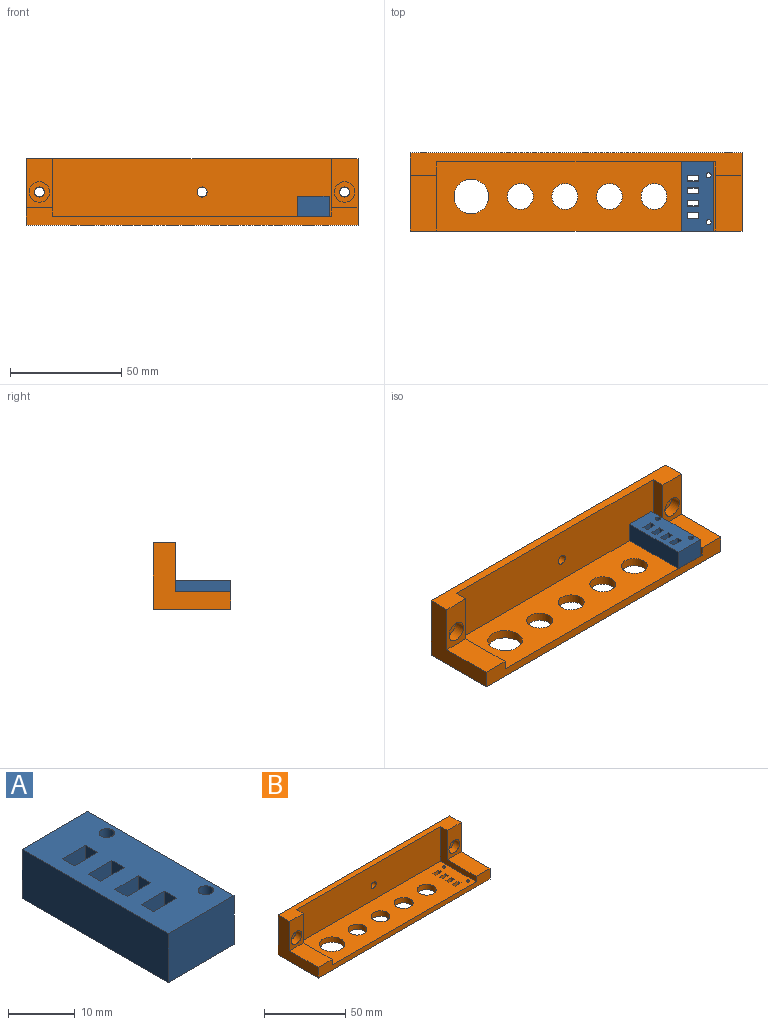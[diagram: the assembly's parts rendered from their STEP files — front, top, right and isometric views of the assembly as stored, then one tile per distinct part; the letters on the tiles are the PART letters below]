
ASSEMBLY  parts=2 mates=1
PART A: 44 faces, bbox 14x31x9 mm
  f0: plane 2.4x1mm, normal (1,0,0), area 2.4mm2, adj f1,f12,f23,f28
  f1: plane 4.8x1mm, normal (0,-1,0), area 4.8mm2, adj f0,f2,f23,f28
  f2: plane 2.4x1mm, normal (-1,0,0), area 2.4mm2, adj f1,f12,f23,f28
  f3: plane 2.4x1mm, normal (1,0,0), area 2.4mm2, adj f4,f13,f23,f33
  f4: plane 4.8x1mm, normal (0,-1,0), area 4.8mm2, adj f3,f5,f23,f33
  f5: plane 2.4x1mm, normal (-1,0,0), area 2.4mm2, adj f4,f13,f23,f33
  f6: plane 2.4x1mm, normal (1,0,0), area 2.4mm2, adj f7,f14,f23,f38
  f7: plane 4.8x1mm, normal (0,-1,0), area 4.8mm2, adj f6,f8,f23,f38
  f8: plane 2.4x1mm, normal (-1,0,0), area 2.4mm2, adj f7,f14,f23,f38
  f9: plane 2.4x1mm, normal (1,0,0), area 2.4mm2, adj f10,f15,f23,f43
  f10: plane 4.8x1mm, normal (0,-1,0), area 4.8mm2, adj f9,f11,f23,f43
  f11: plane 2.4x1mm, normal (-1,0,0), area 2.4mm2, adj f10,f15,f23,f43
  f12: plane 4.8x1mm, normal (0,1,0), area 4.8mm2, adj f0,f2,f23,f28
  f13: plane 4.8x1mm, normal (0,1,0), area 4.8mm2, adj f3,f5,f23,f33
  f14: plane 4.8x1mm, normal (0,1,0), area 4.8mm2, adj f6,f8,f23,f38
  f15: plane 4.8x1mm, normal (0,1,0), area 4.8mm2, adj f9,f11,f23,f43
  f16: plane 31x14mm, normal (0,0,1), area 373.7mm2, adj f17,f18,f19,f20,f21,f22,f24,f25
  f17: plane 14x9mm, normal (0,1,0), area 126mm2, adj f16,f18,f22,f23
  f18: plane 31x9mm, normal (-1,0,0), area 279mm2, adj f16,f17,f19,f23
  f19: plane 14x9mm, normal (0,-1,0), area 126mm2, adj f16,f18,f22,f23
  f20: cylinder r=1.15mm len=9mm, axis (0,0,-1), area 65mm2, adj f16,f23
  f21: cylinder r=1.15mm len=9mm, axis (0,0,-1), area 65mm2, adj f16,f23
  f22: plane 31x9mm, normal (1,0,0), area 279mm2, adj f16,f17,f19,f23
  f23: plane 31x14mm, normal (0,0,-1), area 379.6mm2, adj f0,f1,f2,f3,f4,f5,f6,f7
  f24: plane 8x5mm, normal (0,-1,0), area 40mm2, adj f16,f25,f27,f28
  f25: plane 8x2.6mm, normal (1,0,0), area 20.8mm2, adj f16,f24,f26,f28
  f26: plane 8x5mm, normal (0,1,0), area 40mm2, adj f16,f25,f27,f28
  f27: plane 8x2.6mm, normal (-1,0,0), area 20.8mm2, adj f16,f24,f26,f28
  f28: plane 5x2.6mm, normal (0,0,1), area 1.5mm2, adj f0,f1,f2,f12,f24,f25,f26,f27
  f29: plane 8x5mm, normal (0,-1,0), area 40mm2, adj f16,f30,f32,f33
  f30: plane 8x2.6mm, normal (1,0,0), area 20.8mm2, adj f16,f29,f31,f33
  f31: plane 8x5mm, normal (0,1,0), area 40mm2, adj f16,f30,f32,f33
  f32: plane 8x2.6mm, normal (-1,0,0), area 20.8mm2, adj f16,f29,f31,f33
  f33: plane 5x2.6mm, normal (0,0,1), area 1.5mm2, adj f3,f4,f5,f13,f29,f30,f31,f32
  f34: plane 8x5mm, normal (0,-1,0), area 40mm2, adj f16,f35,f37,f38
  f35: plane 8x2.6mm, normal (1,0,0), area 20.8mm2, adj f16,f34,f36,f38
  f36: plane 8x5mm, normal (0,1,0), area 40mm2, adj f16,f35,f37,f38
  f37: plane 8x2.6mm, normal (-1,0,0), area 20.8mm2, adj f16,f34,f36,f38
  f38: plane 5x2.6mm, normal (0,0,1), area 1.5mm2, adj f6,f7,f8,f14,f34,f35,f36,f37
  f39: plane 8x5mm, normal (0,-1,0), area 40mm2, adj f16,f40,f42,f43
  f40: plane 8x2.6mm, normal (1,0,0), area 20.8mm2, adj f16,f39,f41,f43
  f41: plane 8x5mm, normal (0,1,0), area 40mm2, adj f16,f40,f42,f43
  f42: plane 8x2.6mm, normal (-1,0,0), area 20.8mm2, adj f16,f39,f41,f43
  f43: plane 5x2.6mm, normal (0,0,1), area 1.5mm2, adj f9,f10,f11,f15,f39,f40,f41,f42
PART B: 44 faces, bbox 149x35x30 mm
  f0: plane 125x31mm, normal (0,0,1), area 3203.3mm2, adj f4,f5,f6,f7,f8,f9,f10,f11
  f1: plane 22x12mm, normal (0,-1,0), area 197.5mm2, adj f28,f33,f34,f39,f40
  f2: cylinder r=2.25mm len=5mm, axis (0,-1,0), area 70.7mm2, adj f29,f38
  f3: cylinder r=2.25mm len=5mm, axis (0,-1,0), area 70.7mm2, adj f29,f36
  f4: plane 149x8mm, normal (0,-1,0), area 692mm2, adj f0,f26,f30,f32,f33,f34,f40,f41
  f5: plane 4x2.6mm, normal (1,0,0), area 10.4mm2, adj f0,f6,f17,f26
  f6: plane 5x4mm, normal (0,-1,0), area 20mm2, adj f0,f5,f7,f26
  f7: plane 4x2.6mm, normal (-1,0,0), area 10.4mm2, adj f0,f6,f17,f26
  f8: plane 4x2.6mm, normal (1,0,0), area 10.4mm2, adj f0,f9,f18,f26
  f9: plane 5x4mm, normal (0,-1,0), area 20mm2, adj f0,f8,f10,f26
  f10: plane 4x2.6mm, normal (-1,0,0), area 10.4mm2, adj f0,f9,f18,f26
  f11: plane 4x2.6mm, normal (1,0,0), area 10.4mm2, adj f0,f12,f19,f26
  f12: plane 5x4mm, normal (0,-1,0), area 20mm2, adj f0,f11,f13,f26
  f13: plane 4x2.6mm, normal (-1,0,0), area 10.4mm2, adj f0,f12,f19,f26
  f14: plane 4x2.6mm, normal (1,0,0), area 10.4mm2, adj f0,f15,f20,f26
  f15: plane 5x4mm, normal (0,-1,0), area 20mm2, adj f0,f14,f16,f26
  f16: plane 4x2.6mm, normal (-1,0,0), area 10.4mm2, adj f0,f15,f20,f26
  f17: plane 5x4mm, normal (0,1,0), area 20mm2, adj f0,f5,f7,f26
  f18: plane 5x4mm, normal (0,1,0), area 20mm2, adj f0,f8,f10,f26
  f19: plane 5x4mm, normal (0,1,0), area 20mm2, adj f0,f11,f13,f26
  f20: plane 5x4mm, normal (0,1,0), area 20mm2, adj f0,f14,f16,f26
  f21: cylinder r=7.75mm len=15.5mm, axis (0,0,-1), area 194.8mm2, adj f0,f26
  f22: cylinder r=5.8mm len=11.6mm, axis (0,0,-1), area 145.8mm2, adj f0,f26
  f23: cylinder r=5.8mm len=11.6mm, axis (0,0,-1), area 145.8mm2, adj f0,f26
  f24: cylinder r=5.8mm len=11.6mm, axis (0,0,-1), area 145.8mm2, adj f0,f26
  f25: cylinder r=5.8mm len=11.6mm, axis (0,0,-1), area 145.8mm2, adj f0,f26
  f26: plane 149x35mm, normal (0,0,-1), area 4543.3mm2, adj f4,f5,f6,f7,f8,f9,f10,f11
  f27: plane 125x26mm, normal (0,-1,0), area 3234.1mm2, adj f0,f28,f30,f34,f35
  f28: plane 149x10mm, normal (0,0,1), area 740mm2, adj f1,f27,f29,f30,f31,f32,f33,f34
  f29: plane 149x30mm, normal (0,1,0), area 4422.3mm2, adj f2,f3,f26,f28,f32,f33,f35
  f30: plane 31x26mm, normal (-1,0,0), area 256mm2, adj f0,f4,f27,f28,f31,f41
  f31: plane 22x12mm, normal (0,-1,0), area 197.5mm2, adj f28,f30,f32,f37,f41
  f32: plane 35x30mm, normal (1,0,0), area 500mm2, adj f4,f26,f28,f29,f31,f41
  f33: plane 35x30mm, normal (-1,0,0), area 500mm2, adj f1,f4,f26,f28,f29,f40
  f34: plane 31x26mm, normal (1,0,0), area 256mm2, adj f0,f1,f4,f27,f28,f40
  f35: cylinder r=2.25mm len=4.5mm, axis (0,-1,0), area 56.5mm2, adj f27,f29
  f36: plane 9.2x9.2mm, normal (0,-1,0), area 50.6mm2, adj f3,f37
  f37: cylinder r=4.6mm len=9.2mm, axis (0,-1,0), area 144.5mm2, adj f31,f36
  f38: plane 9.2x9.2mm, normal (0,-1,0), area 50.6mm2, adj f2,f39
  f39: cylinder r=4.6mm len=9.2mm, axis (0,-1,0), area 144.5mm2, adj f1,f38
  f40: plane 25x12mm, normal (0,0,1), area 300mm2, adj f1,f4,f33,f34
  f41: plane 25x12mm, normal (0,0,1), area 300mm2, adj f4,f30,f31,f32
  f42: cylinder r=1.15mm len=4mm, axis (0,0,-1), area 28.9mm2, adj f0,f26
  f43: cylinder r=1.15mm len=4mm, axis (0,0,-1), area 28.9mm2, adj f0,f26
PLACE A t=(40.66,9.79,-10.64)mm
PLACE B t=(-69.34,9.79,-14.64)mm
MATE fastened A.f20 <-> B.f43  axis (0,0,-1) through (52.66,3.79,-10.64)mm
